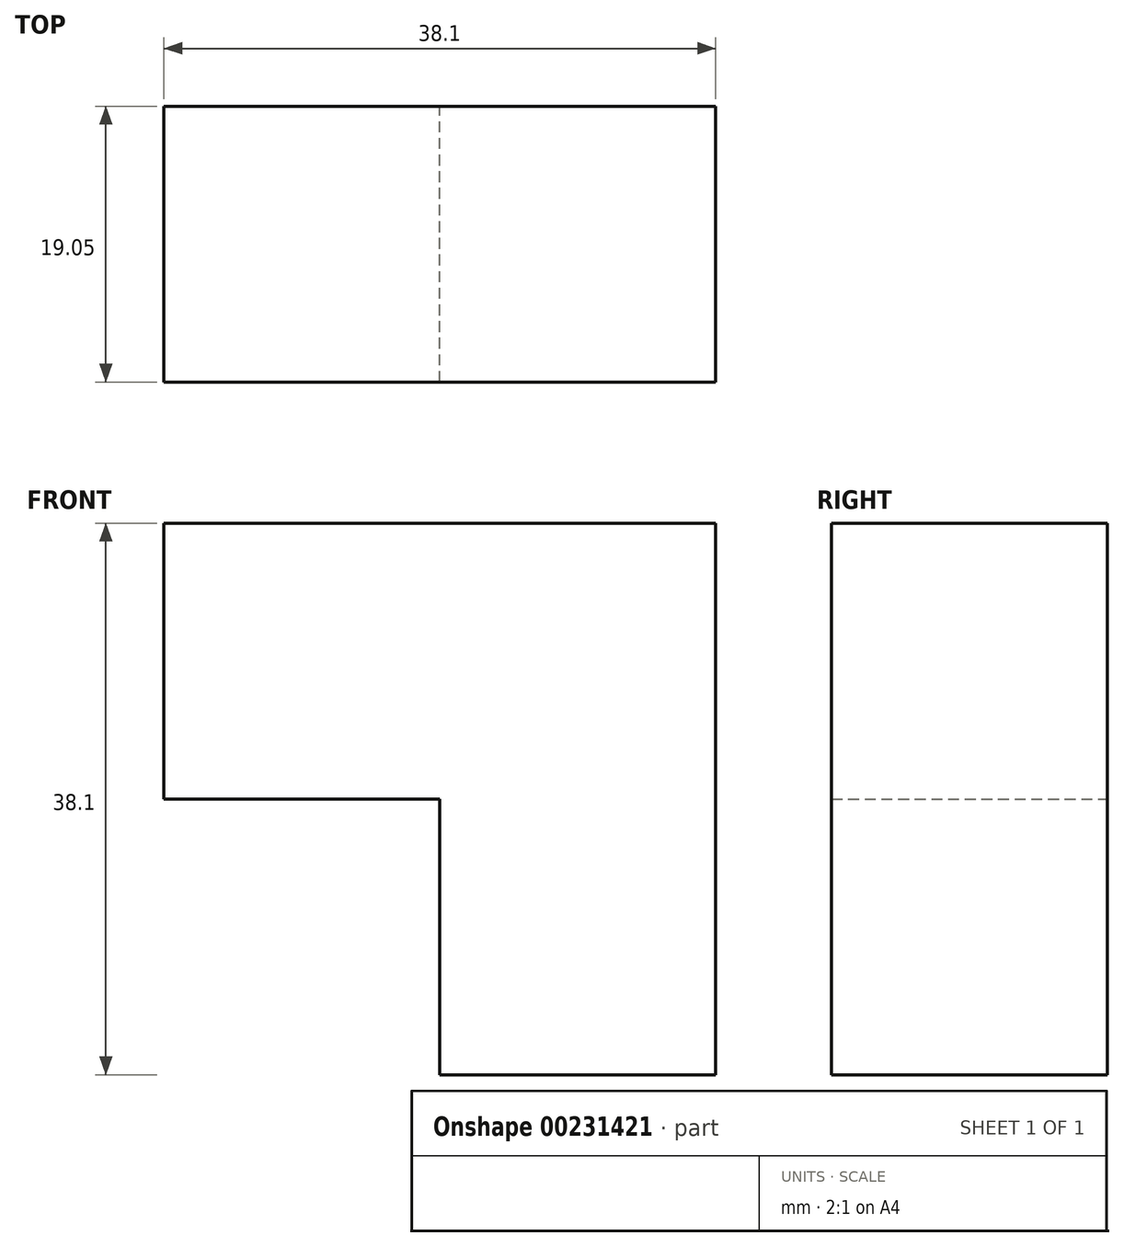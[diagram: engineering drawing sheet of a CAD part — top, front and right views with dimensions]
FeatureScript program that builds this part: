
annotation { "Feature Type Name" : "Feature", "Feature Type Description" : "" }
export const myFeature = defineFeature(function(context is Context, id is Id, definition is map)
    precondition{}
    {
        {
            var Q0;
            Q0=qCreatedBy(makeId("Front.planeOp"),FACE);
            var sketch = newSketch(context, id + "F0", { "sketchPlane" : qUnion([Q0])});
            skLineSegment(sketch, "E0.bottom", {"start": v(-32.42, 38.94) * mm, "end": v(5.68, 38.94) * mm});
            skLineSegment(sketch, "E0.top", {"start": v(-32.42, 19.89) * mm, "end": v(5.68, 19.89) * mm});
            skLineSegment(sketch, "E0.left", {"start": v(-32.42, 38.94) * mm, "end": v(-32.42, 19.89) * mm});
            skLineSegment(sketch, "E0.right", {"start": v(5.68, 38.94) * mm, "end": v(5.68, 19.89) * mm});
            skLineSegment(sketch, "E1.bottom", {"start": v(5.68, 19.89) * mm, "end": v(-13.37, 19.89) * mm});
            skLineSegment(sketch, "E1.top", {"start": v(5.68, 0.84) * mm, "end": v(-13.37, 0.84) * mm});
            skLineSegment(sketch, "E1.left", {"start": v(5.68, 19.89) * mm, "end": v(5.68, 0.84) * mm});
            skLineSegment(sketch, "E1.right", {"start": v(-13.37, 19.89) * mm, "end": v(-13.37, 0.84) * mm});
            skSolve(sketch);
        }
        {
            var Q0;
            Q0 = qSketchRegion(id + "F0", true);
            extrude(context, id + "F1", {"entities" : qUnion([Q0]), "depth" : 19.05 * mm});
        }
    });
